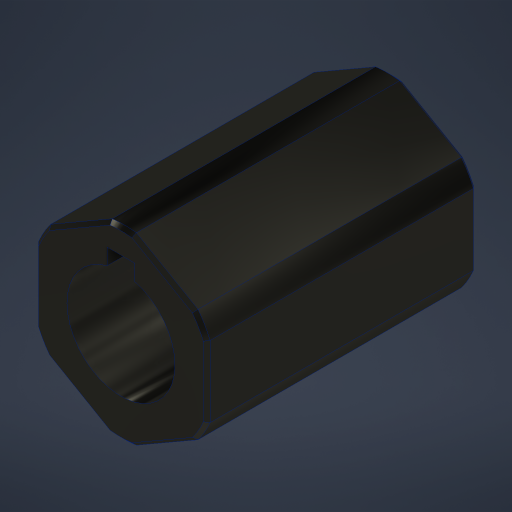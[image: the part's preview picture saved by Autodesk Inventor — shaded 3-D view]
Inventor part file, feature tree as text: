
AUTODESK INVENTOR PART (.ipt)
format: ipt  version: 2024 (Build 280153000, 153)  size: 218,112 bytes
history: native  units: in
note: dims shown in document units (in); Inventor stores cm internally (conversion verified against a paired STEP export)
features: chamfer x1
ambient origin geometry x8: Origin, YZ Plane, XZ Plane, XY Plane, X Axis, Y Axis, Z Axis, Center Point
bodies: Solid1 (feature_tree)
feature tree (1):
  chamfer  "Chamfer1"  [1 undecoded]
note: 1 required parameter value undecoded (feature->parameter linkage not recoverable at this tier; creation-order binding heuristic only, values carry confidence <= 0.55)
